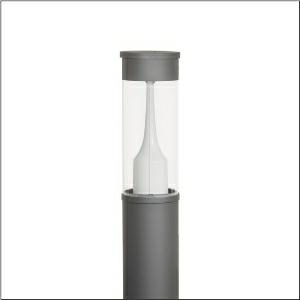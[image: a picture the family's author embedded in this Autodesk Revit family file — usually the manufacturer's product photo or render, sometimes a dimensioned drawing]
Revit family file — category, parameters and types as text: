
# Revit family: city-light_260_iq___p1_0a_5xa5295ff14h_c360
name_source: partatom
category: Lighting Fixtures
units: mm (PartAtom-declared; Revit-internal decimal feet)

## family parameters
Cut with Voids When Loaded = No
Host = Face
Light Source = No
Part Type = Normal
Room Calculation Point = No
Round Connector Dimension = Use Diameter
Shared = No

## types (1)
- --- (1 x LED, 1510 lm, 10.5 W, 3000K)
    Apparent Load = 11 VA
    CIE Flux Codes = 32 61 90 93 100
    Color Rendering = 70
    Color Temperature = 3000K
    Default Elevation = 1800 mm
    Description = City-Light 260 iQ, light pillar, Module 540 iQ-SR, primary light control with 3 zone facetted reflector, of plastic, silver coated, highly specular, structured, primary optical cover: cover, of PMMA, transparent, light distribution: P1.0a, primary light characteristic: strongly asymmetric, LED, High Power LED, rated luminous flux: 1.510lm, luminous efficacy: 144lm/W, light colour: 730, colour temperature: 3000K, control gear: iQ Street-Remote, control: Auto-Match, Temp-Guard, Lumen-Switch, Night-Set, Smart-Wire, Light-Fading, Desk-Remote (wireless, voltage-free reading and setting of iQ features in the workshop via application-optimized NFC function/RFID function), optimised constant luminous flux control (CLO 2.0), Street-Remote, pre-setting: logarithmic dimming characteristic, with terminal, 6-pole, max. 2.5mm², mains connection: 230..240V, AC, 50/60Hz, start of lifetime: 11W, end of service life: 11W, reduction: 5W, luminaire housing, cylindrical, of extruded aluminium section, coated, Siteco® metallic grey (DB 702S), length: 2.600mm, diameter: 200mm, Module 540 iQ-SR, traffic white (RAL 9016), equipment: standard, protection rating (complete): IP65, insulation class (complete): insulation class II (safety insulation), certification: CE, ENEC, VDE, packaging unit: 1 piece

Light Distribution: P1.0a
    Height = 500 mm
    Lamp = 1 x LED
    Lamp Light Flux = 1510 lm
    Lamp Power = 10.5 W
    Lamp count = 1
    Length = 200 mm  [stored 0.656168 ft]
    Luminous efficacy = 144 lm/W
    Manufacturer = Siteco
    ModVariant = No
    Model = 5XA5295FF14H
    Mounting Place = Floor
    Mounting Type = Freestanding
    Number of Poles = 1
    OnlyDefault = Yes
    Power Factor = 1
    Product Name = City-Light 260 iQ | P1.0a
    Product group = light pillar
    ProductGroupID = 1301
    Protection Class = Protection class II
    Protection Degree = IP 65
    RLX_Detail_Level = 1
    RLX_Emergency_Light_Flux = 0 lm
    RLX_Emergency_Type = 0
    RLX_Emergency_Type_DB = No
    RlxData = <blob elided: 52645 chars, md5=f635cb93>
    Socket = socket
    Standby Power = 0 W
    System Light Flux = 1510 lm
    System Power = 11 W
    Type Comments = factory setting: luminous flux: 100 % | dim-lin: 254 | 419 mA
    Type Image = l_1006918.jpg
    URL = http://relux.com
    VarID = @adj_158975
    Voltage = 0 V
    Weight = 0.00 kg
    Width = 0 mm  [stored 0 ft]

note: [stored X ft] marks values corroborated as IEEE doubles in the binary element streams (Revit-internal decimal feet)

## geometry (parser evidence)
native form markers: Blend x4, Sweep x11
no freeform markers — native parametric forms only
